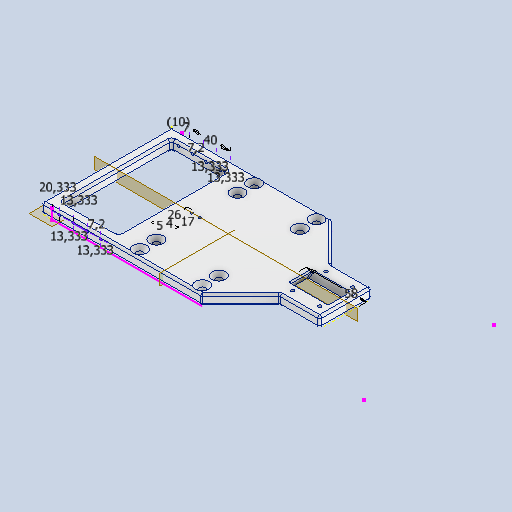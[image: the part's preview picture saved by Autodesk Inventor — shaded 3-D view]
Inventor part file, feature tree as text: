
AUTODESK INVENTOR PART (.ipt)
format: ipt  version: 2025 (Build 290162010, 162A)  size: 606,208 bytes
history: native  units: mm
features: sketch x14, hole x8, other x8, fillet x7, reference x6, extrude x5, projected_geometry x5, plane x4, chamfer x2, mirror x1, loft x1
ambient origin geometry x8: Origin, YZ Plane, XZ Plane, XY Plane, X Axis, Y Axis, Z Axis, Center Point
bodies: Volumenkörper1 (feature_tree)
feature tree (61):
  extrude  "main"  Depth=125.0mm
  hole  "BohrungLin"  [1 undecoded]
  plane  "Arbeitsebene4"
  extrude  "Extrusion7"  Depth=2.0mm
  fillet  "Rundung1"  Radius=77.0mm
  chamfer  "Fasen1"  Distance=3.5mm
  extrude  "Extrusion8"  Depth=2.0mm
  plane  "Arbeitsebene1"
  mirror  "Spiegeln1"
  plane  "Arbeitsebene2"
  hole  "Bohrung7"  [1 undecoded]
  loft  "Erhebung1"
  hole  "Bohrung10"  [1 undecoded]
  chamfer  "Fasen2"  Distance=2.0mm
  hole  "Bohrung11"  [1 undecoded]
  hole  "Bohrung12"  [1 undecoded]
  fillet  "Rundung5"  [1 undecoded]
  fillet  "Rundung6"  Radius=74.0mm
  fillet  "Rundung7"  Radius=16.0mm
  fillet  "Rundung8"  Radius=16.0mm
  fillet  "Rundung9"  Radius=70.0mm
  plane  "Arbeitsebene5"
  extrude  "Extrusion11"  Depth=2.0mm
  hole  "SeildurchgangL"  [1 undecoded]
  hole  "SeildurchgangR"  [1 undecoded]
  fillet  "Rundung10"  Radius=16.0mm
  sketch  "Skizze29"  dims[d128=20.0mm d129=3.5mm d130=0.0mm d131=2.5mm d132=1.0mm d133=2.0mm d134=45.0deg d135=2.0mm d136=1.0mm d137=2.0mm d138=5.0mm d139=0.0mm d154=1.567mm d155=5.0mm d156=4.0mm d157=2.0mm d158=90.0deg d159=6.3mm d160=20.594885mm d208=0.0mm d209=90.0deg d210=0.0mm d211=90.0deg d220=74.0mm d221=16.0mm d222=16.0mm d223=70.0mm d224=50.0mm d225=16.0mm d226=16.0mm d227=16.0mm d228=16.0mm d229=41.95mm d230=6.779mm d231=8.0mm d232=2.459mm d233=6.0mm d234=13.0mm d235=2.0mm d236=90.0deg d237=11.8mm d238=20.594885mm d242=37.5mm d243=2.0mm d244=45.0deg d245=40.0mm d246=32.0mm d247=26.0mm d248=2.0mm d249=3.242mm d250=8.0mm d251=4.0mm d252=2.0mm d253=90.0deg d254=8.0mm d255=20.594885mm d257=22.0mm d259=14.0mm d261=2.0mm d264=30.0mm d265=20.0mm d266=1.567mm d267=5.0mm d268=6.3mm d269=2.0mm d270=90.0deg d271=6.3mm d272=20.594885mm d273=2.0mm d274=22.0mm d275=20.207259mm d276=14.871377mm d277=3.0mm d278=25.980762mm d279=17.550869mm d280=1.0mm d281=1.0mm d282=1.0mm d283=1.0mm d284=10.0mm d285=10.0mm d286=10.3335mm d287=53.332mm d288=10.334mm d289=10.334mm d290=0.0mm d291=0.0mm d292=13.333mm d293=13.333mm d294=13.333mm d295=13.333333mm d296=2.0mm d297=42.0mm d298=14.0mm d299=62.5mm d300=26.0mm d301=5.0mm d302=58.0mm d303=5.0mm d304=0.0mm d305=17.0mm d306=4.0mm d307=1.567mm d308=4.0mm d309=10.4mm d310=2.0mm d311=90.0deg d312=9.0mm d313=20.594885mm]
  extrude  "Extrusion12"  Depth=2.0mm
  hole  "Bohrung13"  [1 undecoded]
  sketch  "Skizze1"  dims[d0=220.0mm d1=125.0mm]
  sketch  "Skizze2"  dims[d3=10.0mm d4=0.0mm d30=60.0mm]
  sketch  "Skizze4"  dims[d31=6.0mm d32=6.0mm d33=13.0mm d34=2.0mm d35=90.0deg d36=8.0mm d37=20.594885mm]
  sketch  "Skizze8"  dims[d50=2.459mm d51=1.0mm d52=4.0mm d53=2.0mm d54=90.0deg d55=1.0mm d56=20.594885mm]
  sketch  "Skizze12"  dims[d79=2.459mm d80=1.0mm d81=4.0mm d82=2.0mm d83=90.0deg d84=1.0mm d85=20.594885mm d88=7.5mm d89=77.0mm]
  projected_geometry  "Projizierte Kontur2"
  sketch  "Skizze13"  dims[d95=7.2mm]
  sketch  "Skizze15"  dims[d97=7.0mm]
  reference  "Referenz14"
  reference  "Referenz16"
  sketch  "Skizze22"  dims[d98=40.0mm]
  sketch  "Skizze23"  dims[d117=7.2mm]
  sketch  "Skizze25"  dims[d118=20.333333mm]
  sketch  "Skizze26"  dims[d120=13.333333mm]
  reference  "Referenz46"
  sketch  "Skizze27"  dims[d125=21.0mm]
  reference  "Referenz47"
  sketch  "Skizze28"  dims[d126=5.0mm]
  projected_geometry  "Projizierte Kontur3"
  projected_geometry  "Projizierte Kontur4"
  projected_geometry  "Projizierte Kontur5"
  projected_geometry  "Projizierte Kontur6"
  reference  "Referenz48"
  reference  "Referenz49"
  other  "<userpath>\GIT\HDVKBM\CAD\Krandemonstrator\Schlitten.iam"
  other  "Schlitten.iam"
  other  "DIN EN ISO 10642 M6  x  16:2"
  other  "DIN EN ISO 10642 M6  x  16:1"
  other  "Bedienhebel:1"
  other  "HebelhalterBlockBlind:1"
  other  "ISO 12633-2 - 20x20x2 - 200:1"
  other  "Sliderhalterpress:3"
note: 9 required parameter values undecoded (feature->parameter linkage not recoverable at this tier; creation-order binding heuristic only, values carry confidence <= 0.55)
